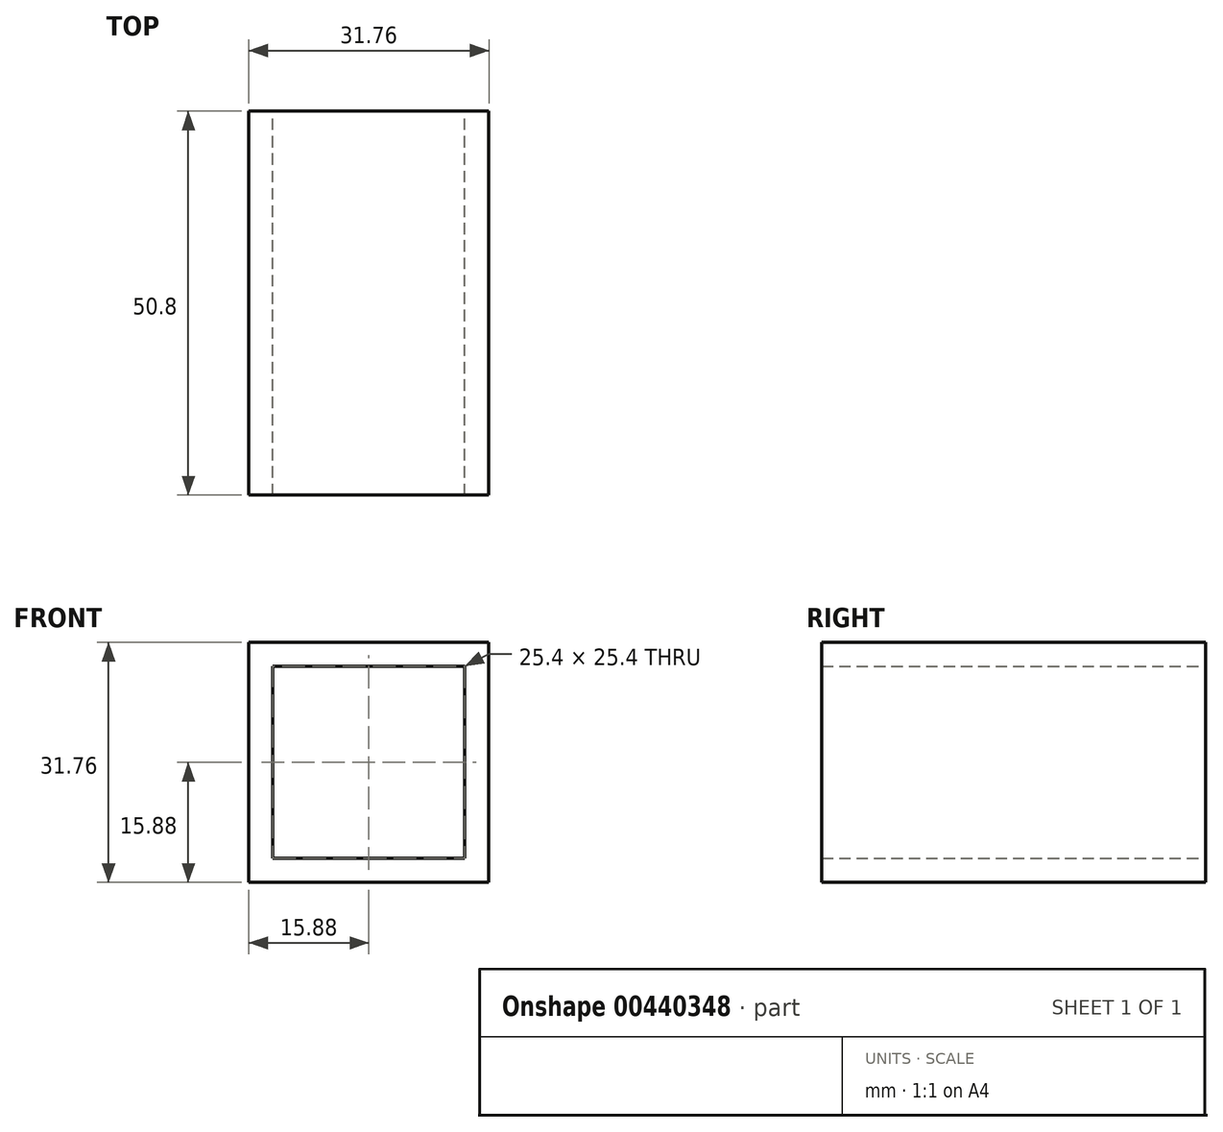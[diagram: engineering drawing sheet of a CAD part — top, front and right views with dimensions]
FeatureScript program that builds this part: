
annotation { "Feature Type Name" : "Feature", "Feature Type Description" : "" }
export const myFeature = defineFeature(function(context is Context, id is Id, definition is map)
    precondition{}
    {
        {
            var Q0;
            Q0=qCreatedBy(makeId("Front.planeOp"),FACE);
            var sketch = newSketch(context, id + "F0", { "sketchPlane" : qUnion([Q0])});
            skLineSegment(sketch, "E0.bottom", {"start": v(-15.88, 15.88) * mm, "end": v(15.88, 15.88) * mm});
            skLineSegment(sketch, "E0.top", {"start": v(-15.88, -15.88) * mm, "end": v(15.87, -15.88) * mm});
            skLineSegment(sketch, "E0.left", {"start": v(-15.87, 15.88) * mm, "end": v(-15.88, -15.88) * mm});
            skLineSegment(sketch, "E0.right", {"start": v(15.88, 15.88) * mm, "end": v(15.87, -15.88) * mm});
            skPoint(sketch, "E0.middle", {"position": v(0, 0) * mm});
            skLineSegment(sketch, "E1.bottom", {"start": v(-12.7, 12.7) * mm, "end": v(12.7, 12.7) * mm});
            skLineSegment(sketch, "E1.top", {"start": v(-12.7, -12.7) * mm, "end": v(12.7, -12.7) * mm});
            skLineSegment(sketch, "E1.left", {"start": v(-12.7, 12.7) * mm, "end": v(-12.7, -12.7) * mm});
            skLineSegment(sketch, "E1.right", {"start": v(12.7, 12.7) * mm, "end": v(12.7, -12.7) * mm});
            skSolve(sketch);
        }
        {
            var Q0;
            Q0=makeQuery(id+"F0.imprint","IMPRINT",FACE,{"disambiguationData":[TD([[makeQuery(id+"F0.imprint","IMPRINT",EDGE,{"derivedFrom":sQuery(id+"F0.wireOp",EDGE,"E0.bottom")}),-1.0]])]});
            extrude(context, id + "F1", {"entities" : qUnion([Q0]), "endBound" : BoundingType.SYMMETRIC, "depth" : 50.8 * mm});
        }
    });
